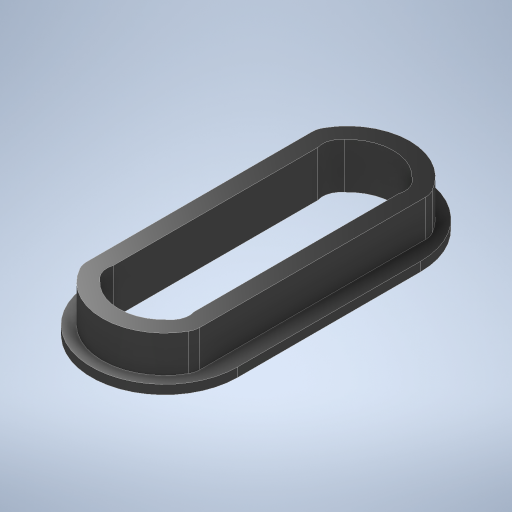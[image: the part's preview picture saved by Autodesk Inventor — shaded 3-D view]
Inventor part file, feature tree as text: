
AUTODESK INVENTOR PART (.ipt)
format: ipt  version: 2024.2 (Build 282272000, 272)  size: 297,984 bytes
history: native  units: mm
features: extrude x2, sketch x1, fillet x1
ambient origin geometry x8: Origin, YZ Plane, XZ Plane, XY Plane, X Axis, Y Axis, Z Axis, Center Point
bodies: Solid1 (feature_tree)
feature tree (4):
  sketch  "Sketch1"  dims[d0=14.0mm d1=2.0mm d2=1.0mm d3=20.0mm d4=8.8mm d5=12.5mm d7=1.85mm d8=5.0mm d9=5.0mm d10=0.0mm d11=1.0mm d12=0.0mm d13=2.0mm d14=0.05mm d15=0.05mm]
  extrude  "Extrusion1"  Depth=2.0mm
  extrude  "Extrusion2"  Depth=8.8mm
  fillet  "Fillet1"  Radius=12.5mm
